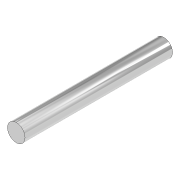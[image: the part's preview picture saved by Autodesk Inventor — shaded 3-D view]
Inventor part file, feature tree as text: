
AUTODESK INVENTOR PART (.ipt)
format: ipt  version: 2020 (Build 240168000, 168)  size: 77,824 bytes
history: native  units: in
note: dims shown in document units (in); Inventor stores cm internally (conversion verified against a paired STEP export)
features: extrude x1, sketch x1
ambient origin geometry x8: Origin, YZ Plane, XZ Plane, XY Plane, X Axis, Y Axis, Z Axis, Center Point
bodies: Solid1 (feature_tree)
feature tree (2):
  extrude  "Extrusion1"  Depth=1.6535in TaperAngle=0.0deg
  sketch  "Sketch1"  dims[d0=0.1969in d1=1.6535in d2=0.0in]
